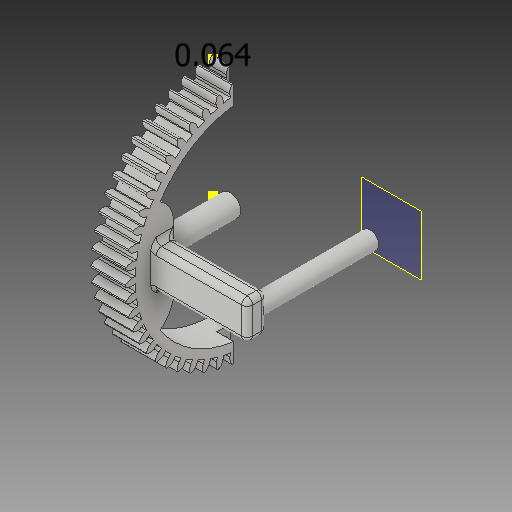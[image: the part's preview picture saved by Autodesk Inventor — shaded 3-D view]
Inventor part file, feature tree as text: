
AUTODESK INVENTOR PART (.ipt)
format: ipt  version: 2018 (Build 220112000, 112)  size: 968,704 bytes
history: native  units: in
note: dims shown in document units (in); Inventor stores cm internally (conversion verified against a paired STEP export)
features: extrude x13, sketch x11, other x6, plane x6, fillet x5, reference x2, projected_geometry x1
ambient origin geometry x8: Origin, YZ Plane, XZ Plane, XY Plane, X Axis, Y Axis, Z Axis, Center Point
bodies: Body1 (feature_tree)
feature tree (44):
  other  "main sketch"
  extrude  "teeth extrude"  Depth=3.25in
  extrude  "other teeth extrude"  Depth=1.2025in
  other  "axel work plane"
  extrude  "axel extrude"  Depth=0.5in TaperAngle=0.0deg
  plane  "Work Plane7"
  extrude  "Extrusion15"  Depth=0.24in
  sketch  "Sketch10"  dims[d13=20.4724in d15=360.0deg d19=0.5in d20=0.0in]
  extrude  "Extrusion16"  Depth=0.311in
  plane  "Work Plane9"
  extrude  "Extrusion18"  Depth=0.0025in
  plane  "Work Plane8"
  extrude  "Extrusion19"  Depth=0.1969in
  extrude  "Extrusion20"  Depth=0.3937in TaperAngle=0.0deg
  extrude  "Extrusion22"  Depth=3.937in TaperAngle=0.0deg
  extrude  "Extrusion23"  Depth=0.29in
  plane  "Work Plane10"
  extrude  "Extrusion26"  Depth=0.0787in TaperAngle=0.0deg
  sketch  "Sketch20"  dims[d97=0.315in d98=0.29in]
  plane  "Work Plane11"
  extrude  "Extrusion28"  Depth=0.0787in TaperAngle=0.0deg
  extrude  "Extrusion29"  Depth=0.0787in
  plane  "Work Plane12"
  fillet  "Fillet8"  Radius=0.3937in
  fillet  "Fillet9"  Radius=0.1489in
  fillet  "Fillet10"  Radius=0.3937in
  fillet  "Fillet11"  Radius=0.0787in
  fillet  "Fillet13"  Radius=0.0787in
  sketch  "Sketch7"  dims[d0=3.0in d1=3.25in]
  sketch  "Sketch9"  dims[d7=1.2025in d8=1.2025in]
  sketch  "Sketch11"  dims[d23=0.5in d24=0.0in d65=0.24in]
  sketch  "Sketch12"  dims[d66=1.3in d67=0.0in d70=0.311in]
  sketch  "Sketch13"  dims[d71=1.4774in d72=0.0in d73=0.0025in]
  sketch  "Sketch15"  dims[d74=1.4774in d75=0.0in d78=0.1969in d79=0.25in]
  sketch  "Sketch16"  dims[d80=39.3701in d81=0.1969in d82=0.0in d83=0.0in d84=0.3937in d85=0.0in]
  sketch  "Sketch19"  dims[d86=3.937in d87=0.0in d93=3.937in d94=0.0in]
  reference  "Reference2"
  sketch  "Sketch21"  dims[d99=0.6299in d100=2.0in d101=0.0in d107=0.75in d108=0.0in d115=0.25in d116=0.3937in d117=0.0in d118=0.1489in d119=0.3937in d120=0.0in d127=0.0787in d128=0.0787in d129=0.0787in d130=0.0787in d132=0.0787in]
  projected_geometry  "Projected Loop1"
  reference  "Reference3"
  other  "<userpath>\OneDrive\Documents\Inventor\TSA\2018\Animatronics\Tortoise\TurtleAssembly.iam"
  other  "TurtleAssembly.iam"
  other  "servo (2):2"
  other  "wheelframe:1"
